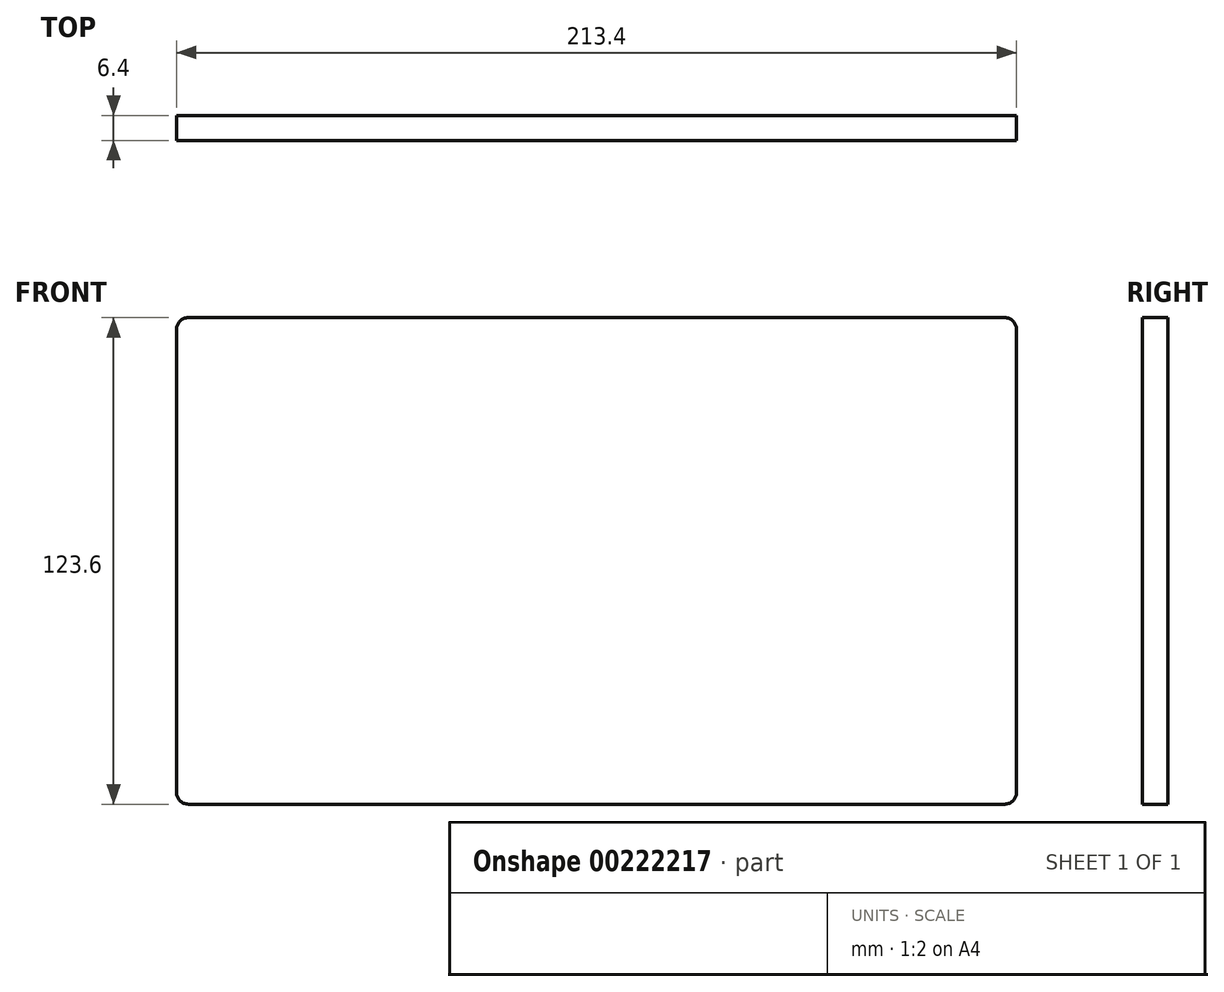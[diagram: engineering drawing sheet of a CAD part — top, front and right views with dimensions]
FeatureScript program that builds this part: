
annotation { "Feature Type Name" : "Feature", "Feature Type Description" : "" }
export const myFeature = defineFeature(function(context is Context, id is Id, definition is map)
    precondition{}
    {
        {
            var Q0;
            Q0=qCreatedBy(makeId("Front.planeOp"),FACE);
            var sketch = newSketch(context, id + "F0", { "sketchPlane" : qUnion([Q0])});
            skLineSegment(sketch, "E0.bottom", {"start": v(-106.7, 61.8) * mm, "end": v(106.7, 61.8) * mm});
            skLineSegment(sketch, "E0.top", {"start": v(-106.7, -61.8) * mm, "end": v(106.7, -61.8) * mm});
            skLineSegment(sketch, "E0.left", {"start": v(-106.7, 61.8) * mm, "end": v(-106.7, -61.8) * mm});
            skLineSegment(sketch, "E0.right", {"start": v(106.7, 61.8) * mm, "end": v(106.7, -61.8) * mm});
            skPoint(sketch, "E1", {"position": v(0, 61.8) * mm});
            skPoint(sketch, "E2", {"position": v(106.7, 0) * mm});
            skSolve(sketch);
        }
        {
            var Q0;
            Q0=makeQuery(id+"F0.imprint","IMPRINT",FACE,{"disambiguationData":[TD([[makeQuery(id+"F0.imprint","IMPRINT",EDGE,{"derivedFrom":sQuery(id+"F0.wireOp",EDGE,"E0.bottom")}),-1.0]])]});
            extrude(context, id + "F1", {"entities" : qUnion([Q0]), "endBound" : BoundingType.SYMMETRIC, "depth" : 6.4 * mm});
        }
        {
            var Q0;
            Q0=makeQuery(id+"F1.opExtrude","SWEPT_EDGE",EDGE,{"disambiguationData":[OSD([sQuery(id+"F0.wireOp",EDGE,"E0.bottom"),sQuery(id+"F0.wireOp",EDGE,"E0.right")])]});
            var Q1;
            Q1=makeQuery(id+"F1.opExtrude","SWEPT_EDGE",EDGE,{"disambiguationData":[OSD([sQuery(id+"F0.wireOp",EDGE,"E0.top"),sQuery(id+"F0.wireOp",EDGE,"E0.right")])]});
            var Q2;
            Q2=makeQuery(id+"F1.opExtrude","SWEPT_EDGE",EDGE,{"disambiguationData":[OSD([sQuery(id+"F0.wireOp",EDGE,"E0.top"),sQuery(id+"F0.wireOp",EDGE,"E0.left")])]});
            var Q3;
            Q3=makeQuery(id+"F1.opExtrude","SWEPT_EDGE",EDGE,{"disambiguationData":[OSD([sQuery(id+"F0.wireOp",EDGE,"E0.bottom"),sQuery(id+"F0.wireOp",EDGE,"E0.left")])]});
            fillet(context, id + "F2", {"entities" : qUnion([Q0, Q1, Q2, Q3]), "radius" : 3 * mm, "tangentPropagation" : true, "allowEdgeOverflow" : false});
        }
    });
